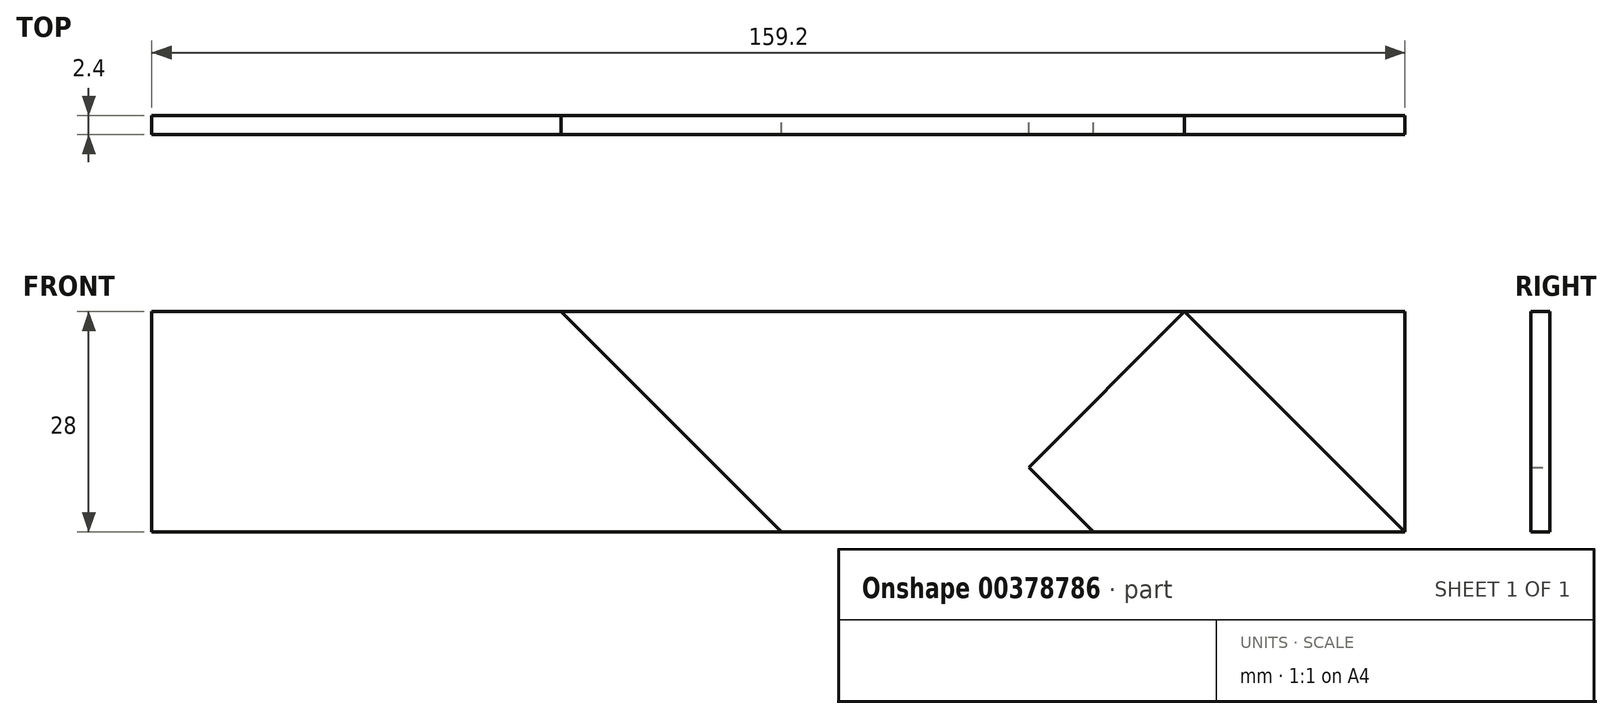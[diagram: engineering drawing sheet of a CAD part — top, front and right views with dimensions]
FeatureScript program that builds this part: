
annotation { "Feature Type Name" : "Feature", "Feature Type Description" : "" }
export const myFeature = defineFeature(function(context is Context, id is Id, definition is map)
    precondition{}
    {
        {
            assignVariable(context, id + "F0", {"name" : "T", "anyValue" : 2.4});
        }
        {
            var Q0;
            Q0=qCreatedBy(makeId("Front.planeOp"),FACE);
            var sketch = newSketch(context, id + "F1", { "sketchPlane" : qUnion([Q0])});
            skLineSegment(sketch, "E0.bottom", {"start": v(0, 0) * mm, "end": v(159.2, 0) * mm});
            skLineSegment(sketch, "E0.top", {"start": v(0, -28) * mm, "end": v(159.2, -28) * mm});
            skLineSegment(sketch, "E0.left", {"start": v(0, 0) * mm, "end": v(0, -28) * mm});
            skLineSegment(sketch, "E0.right", {"start": v(159.2, 0) * mm, "end": v(159.2, -28) * mm});
            skLineSegment(sketch, "E1", {"start": v(52, 0) * mm, "end": v(80, -28) * mm});
            skLineSegment(sketch, "E2", {"start": v(159.2, -28) * mm, "end": v(131.2, 0) * mm});
            skLineSegment(sketch, "E3", {"start": v(131.2, 0) * mm, "end": v(111.4, -19.8) * mm});
            skLineSegment(sketch, "E4", {"start": v(111.4, -19.8) * mm, "end": v(119.6, -28) * mm});
            skSolve(sketch);
        }
        {
            var Q0;
            {var subQ0=sQuery(id+"F1.wireOp",EDGE,"E0.left");Q0=makeQuery(id+"F1.imprint","IMPRINT",FACE,{"disambiguationData":[TD([[makeQuery(id+"F1.imprint","IMPRINT",EDGE,{"derivedFrom":subQ0}),1.0]])]});}
            var Q1;
            {var subQ0=sQuery(id+"F1.wireOp",EDGE,"E2");Q1=makeQuery(id+"F1.imprint","IMPRINT",FACE,{"disambiguationData":[TD([[makeQuery(id+"F1.imprint","IMPRINT",EDGE,{"derivedFrom":subQ0}),1.0]])]});}
            extrude(context, id + "F2", {"entities" : qUnion([Q0, Q1]), "depth" : (getVariable(context, 'T')) * mm});
        }
        {
            var Q0;
            {var subQ1=sQuery(id+"F1.wireOp",EDGE,"E1");Q0=makeQuery(id+"F1.imprint","IMPRINT",FACE,{"disambiguationData":[TD([[makeQuery(id+"F1.imprint","IMPRINT",EDGE,{"derivedFrom":subQ1}),1.0]])]});}
            var Q1;
            {var subQ0=sQuery(id+"F1.wireOp",EDGE,"E0.right");Q1=makeQuery(id+"F1.imprint","IMPRINT",FACE,{"disambiguationData":[TD([[makeQuery(id+"F1.imprint","IMPRINT",EDGE,{"derivedFrom":subQ0}),-1.0]])]});}
            extrude(context, id + "F3", {"entities" : qUnion([Q0, Q1]), "depth" : (getVariable(context, 'T')) * mm});
        }
    });
